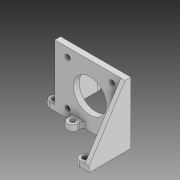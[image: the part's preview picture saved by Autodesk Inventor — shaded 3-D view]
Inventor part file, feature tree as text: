
AUTODESK INVENTOR PART (.ipt)
format: ipt  version: 2020 (Build 240168000, 168)  size: 208,384 bytes
history: native  units: mm
features: extrude x4, sketch x4, fillet x2, projected_geometry x2
ambient origin geometry x8: Origin, YZ Plane, XZ Plane, XY Plane, X Axis, Y Axis, Z Axis, Center Point
bodies: Solid1 (feature_tree)
feature tree (12):
  extrude  "Extrusion1"  Depth=4.0mm TaperAngle=0.0deg
  extrude  "Extrusion2"  Depth=4.0mm
  extrude  "Extrusion3"  Depth=4.0mm
  extrude  "Extrusion4"  Depth=3.0mm TaperAngle=0.0deg
  fillet  "Fillet1"  Radius=3.5mm
  fillet  "Fillet2"  Radius=3.5mm
  sketch  "Sketch1"  dims[d0=23.0mm d1=3.5mm d2=31.0mm d3=31.0mm d4=43.0mm d5=4.0mm d6=0.0mm]
  sketch  "Sketch2"  dims[d7=28.0mm d8=4.0mm]
  projected_geometry  "Projected Loop1"
  sketch  "Sketch3"  dims[d9=3.0mm d10=0.0mm d11=4.0mm]
  projected_geometry  "Projected Loop2"
  sketch  "Sketch4"  dims[d12=25.0mm d13=3.0mm d14=0.0mm d15=3.5mm d16=3.5mm d17=4.0mm d18=0.0mm d19=3.5mm d20=3.5mm d21=3.5mm d22=3.5mm d23=3.5mm d24=3.5mm d25=16.0mm d26=2.0mm d27=25.5mm d28=6.5mm d31=26.5mm d32=19.5mm d33=18.0mm d34=7.0mm d35=25.0mm d36=5.0mm]
